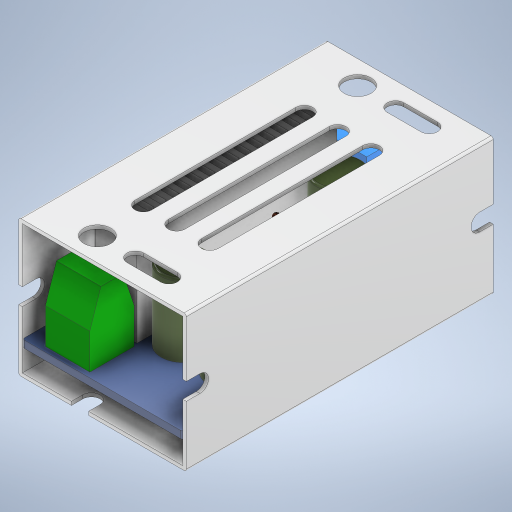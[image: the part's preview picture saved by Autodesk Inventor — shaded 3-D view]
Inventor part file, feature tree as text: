
AUTODESK INVENTOR PART (.ipt)
format: ipt  version: 2024 (Build 280153000, 153)  size: 1,235,456 bytes
history: native  units: in
note: dims shown in document units (in); Inventor stores cm internally (conversion verified against a paired STEP export)
features: extrude x12, sketch x12, fillet x8, other x8, projected_geometry x6, loft x4, plane x2, mirror x1
ambient origin geometry x8: Origin, YZ Plane, XZ Plane, XY Plane, X Axis, Y Axis, Z Axis, Center Point
bodies: Solid1 (feature_tree)
feature tree (53):
  extrude  "Extrusion1"  Depth=2.765in
  extrude  "Extrusion2"  Depth=0.4825in
  fillet  "Fillet2"  Radius=1.8in
  fillet  "Fillet3"  Radius=0.15in
  extrude  "Extrusion3"  Depth=0.15in
  extrude  "Extrusion4"  Depth=0.1in
  extrude  "Extrusion5"  Depth=0.1in
  extrude  "Extrusion6"  Depth=0.1in
  extrude  "Extrusion7"  Depth=0.1in
  extrude  "Extrusion8"  Depth=1.8in
  fillet  "Fillet4"  Radius=0.8125in
  fillet  "Fillet5"  Radius=0.0545in
  fillet  "Fillet6"  Radius=0.0545in
  extrude  "Extrusion9"  Depth=0.0545in
  loft  "Loft1"
  loft  "Loft2"
  loft  "Loft3"
  loft  "Loft4"
  fillet  "Fillet7"  Radius=0.4in
  plane  "Work Plane1"
  extrude  "Extrusion10"  Depth=0.4in
  plane  "Work Plane2"
  sketch  "Sketch12"  dims[d28=0.7in d29=0.3in]
  fillet  "Fillet8"  Radius=0.65in
  extrude  "Extrusion11"  Depth=0.37in
  mirror  "Mirror1"
  extrude  "Extrusion12"  Depth=0.17in
  fillet  "Fillet9"  Radius=0.4in
  sketch  "Sketch1"  dims[d0=1.445in d1=2.765in]
  sketch  "Sketch3"  dims[d2=0.065in d3=0.0in d4=0.4825in d5=1.8in d6=0.15in]
  sketch  "Sketch4"  dims[d7=0.4in d8=0.15in]
  projected_geometry  "Projected Loop1"
  sketch  "Sketch5"  dims[d9=0.1in d10=0.1in]
  sketch  "Sketch6"  dims[d11=0.1in d12=0.1in]
  projected_geometry  "Projected Loop2"
  sketch  "Sketch7"  dims[d13=0.1in d14=0.1in]
  sketch  "Sketch8"  dims[d15=0.1in d16=0.1in]
  sketch  "Sketch9"  dims[d17=0.1in d18=1.8in d19=0.8125in d20=0.0in d22=0.0545in d23=0.0545in]
  projected_geometry  "Projected Loop3"
  sketch  "Sketch10"  dims[d24=0.0545in d25=0.0545in]
  projected_geometry  "Projected Loop4"
  projected_geometry  "Projected Loop5"
  other  "Edges1"
  other  "Edges2"
  other  "Edges3"
  other  "Edges4"
  other  "Edges5"
  other  "Edges6"
  other  "Edges7"
  other  "Edges8"
  sketch  "Sketch11"  dims[d26=0.025in d27=0.025in]
  projected_geometry  "Projected Loop6"
  sketch  "Sketch14"  dims[d30=90.0deg d31=0.7in d32=0.0in d33=0.4in d34=0.0in d35=0.4in d36=0.4in d37=0.65in d38=0.0in d39=0.37in d40=0.17in d41=0.4in d42=0.0in d43=0.4in d44=0.4in d45=0.4in d46=0.4in d47=0.32in d48=0.0in d49=4.7244in d51=360.0deg d53=0.07in d54=0.37in d55=0.0in d56=0.0in d57=0.025in d58=0.025in d59=0.025in d60=0.1in d61=0.1in d62=0.3in d63=0.0in d64=0.0in d65=90.0deg d66=0.0in d67=90.0deg d68=0.0in d69=90.0deg d70=0.0in d71=90.0deg d72=0.0in d73=90.0deg d74=0.0in d75=90.0deg d76=0.0in d77=90.0deg d78=0.0in d79=90.0deg d80=0.02in d81=0.2in d82=0.0325in d83=0.475in d84=0.155in d85=0.18in d86=0.155in d87=0.0325in d88=0.0in d89=-0.7225in d90=0.55in d91=0.2in d92=0.155in d93=0.155in d94=0.2in d95=0.525in d96=0.02in d97=0.0325in d98=0.0in d99=0.3in d100=0.3in d101=0.6368in d102=0.0325in d103=0.0in d104=0.02in]
